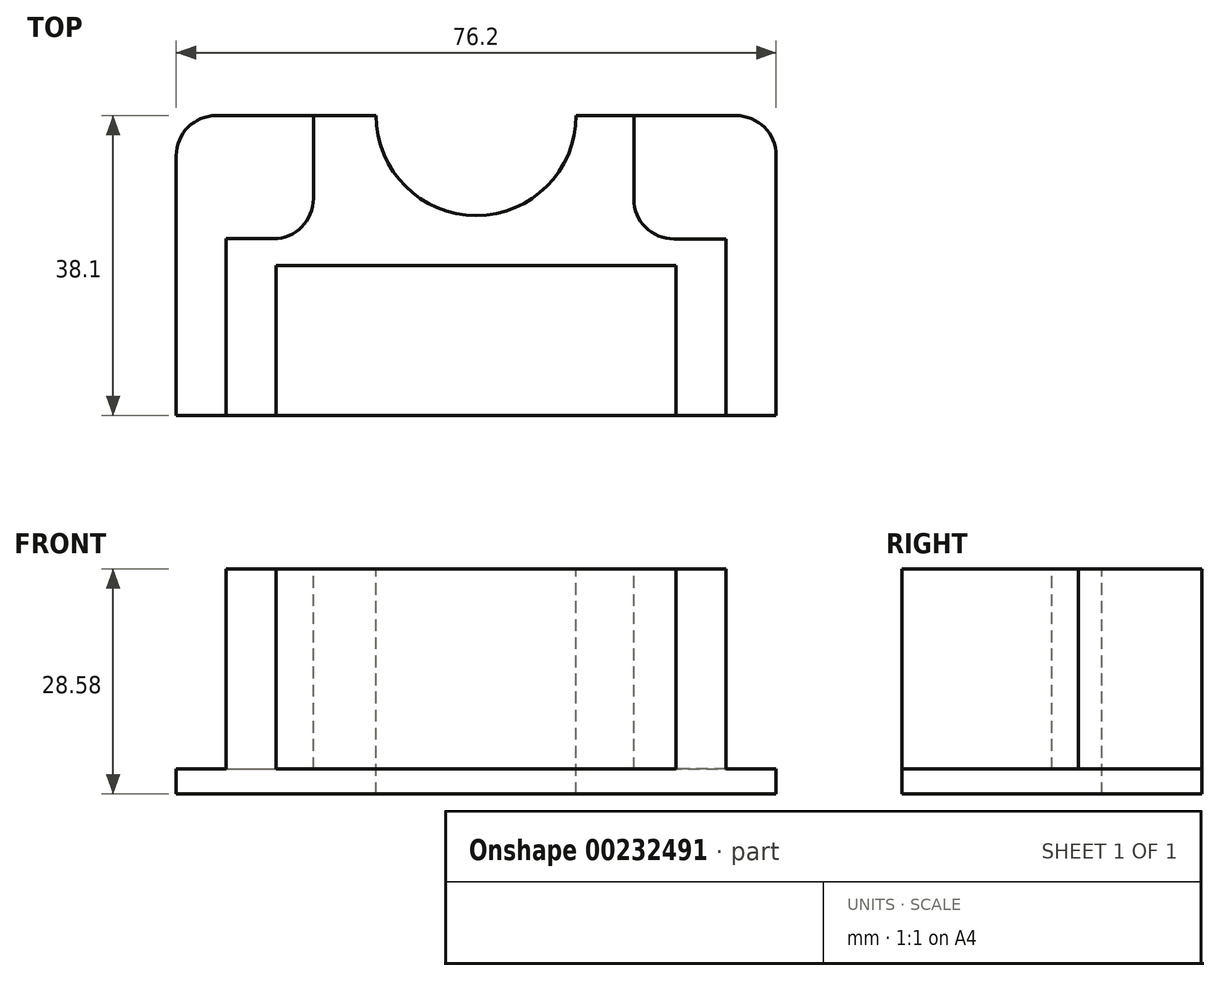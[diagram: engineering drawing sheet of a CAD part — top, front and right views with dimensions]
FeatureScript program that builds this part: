
annotation { "Feature Type Name" : "Feature", "Feature Type Description" : "" }
export const myFeature = defineFeature(function(context is Context, id is Id, definition is map)
    precondition{}
    {
        {
            var Q0;
            Q0=qCreatedBy(makeId("Top.planeOp"),FACE);
            var sketch = newSketch(context, id + "F0", { "sketchPlane" : qUnion([Q0])});
            skLineSegment(sketch, "E0.bottom", {"start": v(-38.1, 19.05) * mm, "end": v(38.1, 19.05) * mm});
            skLineSegment(sketch, "E0.top", {"start": v(-38.1, -19.05) * mm, "end": v(38.1, -19.05) * mm});
            skLineSegment(sketch, "E0.left", {"start": v(-38.1, 19.05) * mm, "end": v(-38.1, -19.05) * mm});
            skLineSegment(sketch, "E0.right", {"start": v(38.1, 19.05) * mm, "end": v(38.1, -19.05) * mm});
            skPoint(sketch, "E0.middle", {"position": v(0, 0) * mm});
            skSolve(sketch);
        }
        {
            var Q0;
            Q0 = qSketchRegion(id + "F0", true);
            extrude(context, id + "F1", {"entities" : qUnion([Q0]), "depth" : 3.17 * mm});
        }
        {
            var Q0;
            Q0=makeQuery(id+"F1.opExtrude","SWEPT_EDGE",EDGE,{"disambiguationData":[OSD([sQuery(id+"F0.wireOp",EDGE,"E0.bottom"),sQuery(id+"F0.wireOp",EDGE,"E0.left")])]});
            var Q1;
            Q1=makeQuery(id+"F1.opExtrude","SWEPT_EDGE",EDGE,{"disambiguationData":[OSD([sQuery(id+"F0.wireOp",EDGE,"E0.bottom"),sQuery(id+"F0.wireOp",EDGE,"E0.right")])]});
            fillet(context, id + "F2", {"entities" : qUnion([Q0, Q1]), "radius" : 5.08 * mm, "tangentPropagation" : true, "allowEdgeOverflow" : false});
        }
        {
            var Q0;
            Q0=makeQuery(id+"F1.opExtrude","CAP_FACE",FACE,{"disambiguationData":[OSD([sQuery(id+"F0.wireOp",EDGE,"E0.bottom"),sQuery(id+"F0.wireOp",EDGE,"E0.top"),sQuery(id+"F0.wireOp",EDGE,"E0.left"),sQuery(id+"F0.wireOp",EDGE,"E0.right")])],"isStart":false});
            var sketch = newSketch(context, id + "F3", { "sketchPlane" : qUnion([Q0])});
            skLineSegment(sketch, "E1.bottom", {"start": v(31.75, -19.05) * mm, "end": v(-31.75, -19.05) * mm});
            skLineSegment(sketch, "E1.top", {"start": v(31.75, 19.05) * mm, "end": v(-31.75, 19.05) * mm});
            skLineSegment(sketch, "E1.left", {"start": v(31.75, -19.05) * mm, "end": v(31.75, 19.05) * mm});
            skLineSegment(sketch, "E1.right", {"start": v(-31.75, -19.05) * mm, "end": v(-31.75, 19.05) * mm});
            skPoint(sketch, "E1.middle", {"position": v(0, 0) * mm});
            skSolve(sketch);
        }
        {
            var Q0;
            Q0=makeQuery(id+"F3.imprint","IMPRINT",FACE,{"disambiguationData":[TD([[makeQuery(id+"F3.imprint","IMPRINT",EDGE,{"derivedFrom":sQuery(id+"F3.wireOp",EDGE,"E1.bottom")}),1.0]])]});
            extrude(context, id + "F4", {"entities" : qUnion([Q0]), "operationType" : NewBodyOperationType.ADD, "depth" : 25.4 * mm});
        }
        {
            var Q0;
            Q0=makeQuery(id+"F4.opExtrude","CAP_FACE",FACE,{"disambiguationData":[OSD([sQuery(id+"F3.wireOp",EDGE,"E1.bottom"),sQuery(id+"F3.wireOp",EDGE,"E1.top"),sQuery(id+"F3.wireOp",EDGE,"E1.left"),sQuery(id+"F3.wireOp",EDGE,"E1.right")])],"isStart":false});
            var sketch = newSketch(context, id + "F5", { "sketchPlane" : qUnion([Q0])});
            skLineSegment(sketch, "E2.bottom", {"start": v(25.4, -19.05) * mm, "end": v(-25.4, -19.05) * mm});
            skLineSegment(sketch, "E2.top", {"start": v(25.4, 0) * mm, "end": v(-25.4, 0) * mm});
            skLineSegment(sketch, "E2.left", {"start": v(25.4, -19.05) * mm, "end": v(25.4, 0) * mm});
            skLineSegment(sketch, "E2.right", {"start": v(-25.4, -19.05) * mm, "end": v(-25.4, 0) * mm});
            skSolve(sketch);
        }
        {
            var Q0;
            Q0 = qSketchRegion(id + "F5", true);
            extrude(context, id + "F6", {"entities" : qUnion([Q0]), "operationType" : NewBodyOperationType.REMOVE, "oppositeDirection" : true, "depth" : 25.4 * mm});
        }
        {
            var Q0;
            Q0=makeQuery(id+"F4.opExtrude","CAP_FACE",FACE,{"disambiguationData":[OSD([sQuery(id+"F3.wireOp",EDGE,"E1.bottom"),sQuery(id+"F3.wireOp",EDGE,"E1.top"),sQuery(id+"F3.wireOp",EDGE,"E1.left"),sQuery(id+"F3.wireOp",EDGE,"E1.right")])],"isStart":false});
            var sketch = newSketch(context, id + "F7", { "sketchPlane" : qUnion([Q0])});
            skCircle(sketch, "E3", {"center": v(0, 19.05) * mm, "radius": 12.7 * mm});
            skSolve(sketch);
        }
        {
            var Q0;
            Q0 = qSketchRegion(id + "F7", true);
            extrude(context, id + "F8", {"entities" : qUnion([Q0]), "operationType" : NewBodyOperationType.REMOVE, "endBound" : BoundingType.THROUGH_ALL, "oppositeDirection" : true, "depth" : 31.75 * mm});
        }
        {
            var Q0;
            Q0=makeQuery(id+"F4.opExtrude","CAP_FACE",FACE,{"disambiguationData":[OSD([sQuery(id+"F3.wireOp",EDGE,"E1.bottom"),sQuery(id+"F3.wireOp",EDGE,"E1.top"),sQuery(id+"F3.wireOp",EDGE,"E1.left"),sQuery(id+"F3.wireOp",EDGE,"E1.right")])],"isStart":false});
            var sketch = newSketch(context, id + "F9", { "sketchPlane" : qUnion([Q0])});
            skLineSegment(sketch, "E4.bottom", {"start": v(-31.75, 19.05) * mm, "end": v(-20.67, 19.05) * mm});
            skLineSegment(sketch, "E4.top", {"start": v(-31.75, 3.41) * mm, "end": v(-20.67, 3.41) * mm});
            skLineSegment(sketch, "E4.left", {"start": v(-31.75, 19.05) * mm, "end": v(-31.75, 3.41) * mm});
            skLineSegment(sketch, "E4.right", {"start": v(-20.67, 19.05) * mm, "end": v(-20.67, 3.41) * mm});
            skSolve(sketch);
        }
        {
            var Q0;
            Q0 = qSketchRegion(id + "F9", true);
            extrude(context, id + "F10", {"entities" : qUnion([Q0]), "operationType" : NewBodyOperationType.REMOVE, "oppositeDirection" : true, "depth" : 25.4 * mm});
        }
        {
            var Q0;
            Q0=makeQuery(id+"F10.boolean.opBoolean","COPY",EDGE,{"derivedFrom":makeQuery(id+"F10.opExtrude","SWEPT_EDGE",EDGE,{"disambiguationData":[OSD([sQuery(id+"F9.wireOp",EDGE,"E4.top"),sQuery(id+"F9.wireOp",EDGE,"E4.right")])]})});
            fillet(context, id + "F11", {"entities" : qUnion([Q0]), "radius" : 5.08 * mm, "tangentPropagation" : true, "allowEdgeOverflow" : false});
        }
        {
            var Q0;
            Q0=makeQuery(id+"F4.opExtrude","CAP_FACE",FACE,{"disambiguationData":[OSD([sQuery(id+"F3.wireOp",EDGE,"E1.bottom"),sQuery(id+"F3.wireOp",EDGE,"E1.top"),sQuery(id+"F3.wireOp",EDGE,"E1.left"),sQuery(id+"F3.wireOp",EDGE,"E1.right")])],"isStart":false});
            var sketch = newSketch(context, id + "F12", { "sketchPlane" : qUnion([Q0])});
            skLineSegment(sketch, "E5.bottom", {"start": v(31.75, 19.05) * mm, "end": v(20.04, 19.05) * mm});
            skLineSegment(sketch, "E5.top", {"start": v(31.75, 3.37) * mm, "end": v(20.04, 3.37) * mm});
            skLineSegment(sketch, "E5.left", {"start": v(31.75, 19.05) * mm, "end": v(31.75, 3.37) * mm});
            skLineSegment(sketch, "E5.right", {"start": v(20.04, 19.05) * mm, "end": v(20.04, 3.37) * mm});
            skSolve(sketch);
        }
        {
            var Q0;
            Q0 = qSketchRegion(id + "F12", true);
            extrude(context, id + "F13", {"entities" : qUnion([Q0]), "operationType" : NewBodyOperationType.REMOVE, "oppositeDirection" : true, "depth" : 25.4 * mm});
        }
        {
            var Q0;
            Q0=makeQuery(id+"F13.boolean.opBoolean","COPY",EDGE,{"derivedFrom":makeQuery(id+"F13.opExtrude","SWEPT_EDGE",EDGE,{"disambiguationData":[OSD([sQuery(id+"F12.wireOp",EDGE,"E5.top"),sQuery(id+"F12.wireOp",EDGE,"E5.right")])]})});
            fillet(context, id + "F14", {"entities" : qUnion([Q0]), "radius" : 5.08 * mm, "tangentPropagation" : true, "allowEdgeOverflow" : false});
        }
    });
